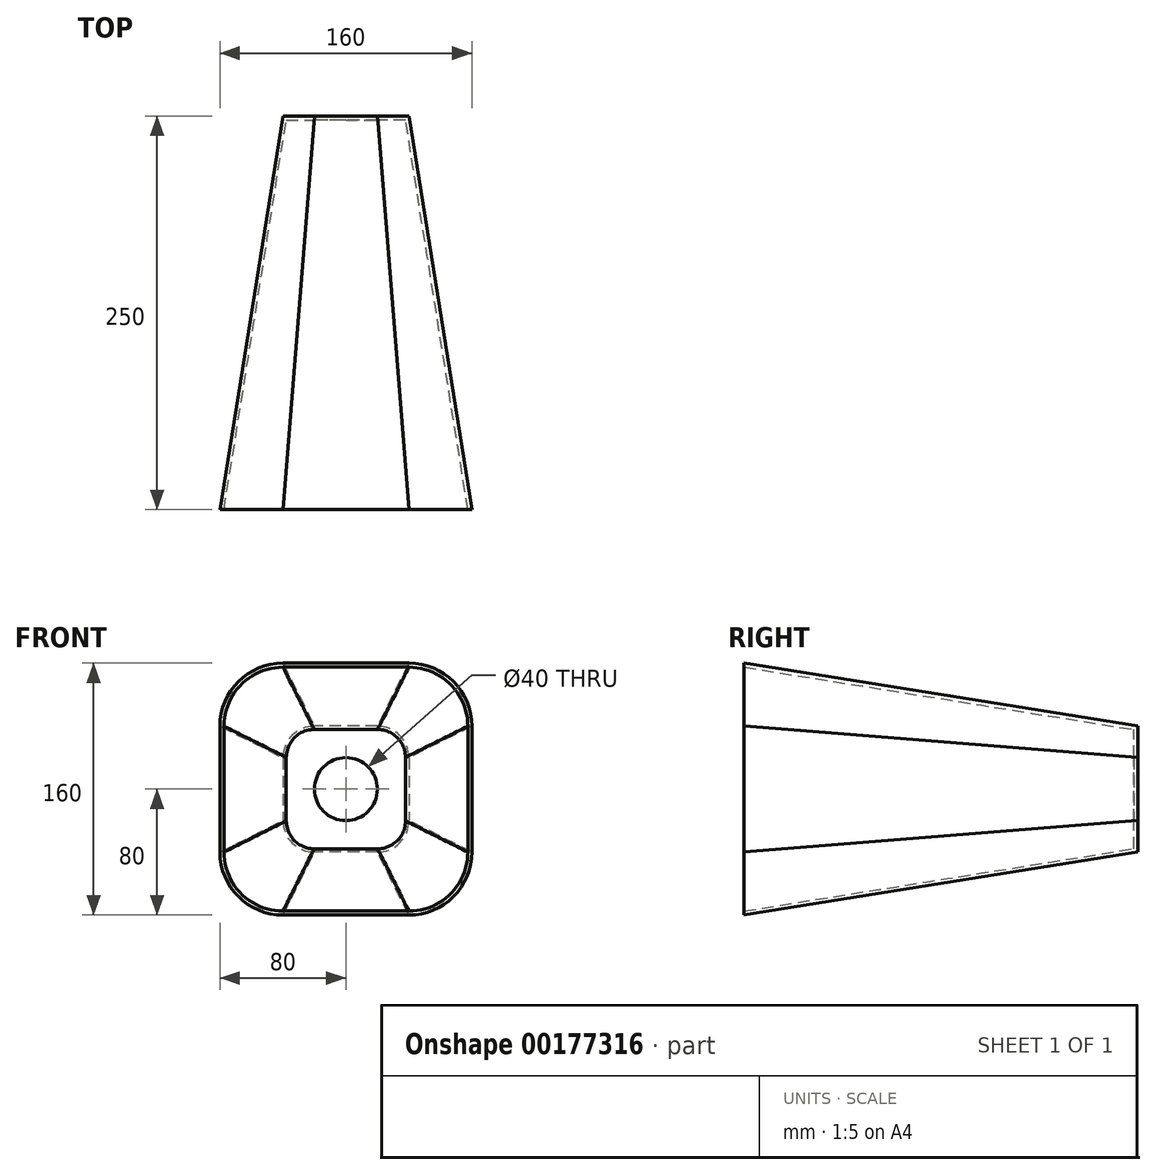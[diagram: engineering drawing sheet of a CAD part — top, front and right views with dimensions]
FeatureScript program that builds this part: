
annotation { "Feature Type Name" : "Feature", "Feature Type Description" : "" }
export const myFeature = defineFeature(function(context is Context, id is Id, definition is map)
    precondition{}
    {
        {
            var Q0;
            Q0=qCreatedBy(makeId("Front.planeOp"),FACE);
            var sketch = newSketch(context, id + "F0", { "sketchPlane" : qUnion([Q0])});
            skLineSegment(sketch, "E0.bottom", {"start": v(20, 40) * mm, "end": v(-20, 40) * mm});
            skLineSegment(sketch, "E0.top", {"start": v(20, -40) * mm, "end": v(-20, -40) * mm});
            skLineSegment(sketch, "E0.left", {"start": v(40, 20) * mm, "end": v(40, -20) * mm});
            skLineSegment(sketch, "E0.right", {"start": v(-40, 20) * mm, "end": v(-40, -20) * mm});
            skPoint(sketch, "E0.middle", {"position": v(0, 0) * mm});
            skPoint(sketch, "E1.visualSharp", {"position": v(-40, 40) * mm});
            skArc(sketch, "E1.filletArc", {"start": v(-20, 40) * mm, "mid": v(-34.14, 34.14) * mm, "end": v(-40, 20) * mm});
            skPoint(sketch, "E2.visualSharp", {"position": v(40, 40) * mm});
            skArc(sketch, "E2.filletArc", {"start": v(40, 20) * mm, "mid": v(34.14, 34.14) * mm, "end": v(20, 40) * mm});
            skPoint(sketch, "E3.visualSharp", {"position": v(40, -40) * mm});
            skArc(sketch, "E3.filletArc", {"start": v(20, -40) * mm, "mid": v(34.14, -34.14) * mm, "end": v(40, -20) * mm});
            skPoint(sketch, "E4.visualSharp", {"position": v(-40, -40) * mm});
            skArc(sketch, "E4.filletArc", {"start": v(-40, -20) * mm, "mid": v(-34.14, -34.14) * mm, "end": v(-20, -40) * mm});
            skSolve(sketch);
        }
        {
            var Q0;
            Q0=qCreatedBy(makeId("Front.planeOp"),FACE);
            cPlane(context, id + "F1", {"entities" : qUnion([Q0]), "cplaneType" : CPlaneType.OFFSET, "offset" : 250 * mm, "width" : 150 * mm, "height" : 150 * mm});
        }
        {
            var Q0;
            Q0=qCreatedBy(id+"F1.planeOp",FACE);
            var sketch = newSketch(context, id + "F2", { "sketchPlane" : qUnion([Q0])});
            skLineSegment(sketch, "E5.bottom", {"start": v(40, 80) * mm, "end": v(-40, 80) * mm});
            skLineSegment(sketch, "E5.top", {"start": v(40, -80) * mm, "end": v(-40, -80) * mm});
            skLineSegment(sketch, "E5.left", {"start": v(80, 40) * mm, "end": v(80, -40) * mm});
            skLineSegment(sketch, "E5.right", {"start": v(-80, 40) * mm, "end": v(-80, -40) * mm});
            skPoint(sketch, "E5.middle", {"position": v(0, 0) * mm});
            skPoint(sketch, "E6.visualSharp", {"position": v(80, 80) * mm});
            skArc(sketch, "E6.filletArc", {"start": v(80, 40) * mm, "mid": v(68.28, 68.28) * mm, "end": v(40, 80) * mm});
            skPoint(sketch, "E7.visualSharp", {"position": v(80, -80) * mm});
            skArc(sketch, "E7.filletArc", {"start": v(40, -80) * mm, "mid": v(68.28, -68.28) * mm, "end": v(80, -40) * mm});
            skPoint(sketch, "E8.visualSharp", {"position": v(-80, -80) * mm});
            skArc(sketch, "E8.filletArc", {"start": v(-80, -40) * mm, "mid": v(-68.28, -68.28) * mm, "end": v(-40, -80) * mm});
            skPoint(sketch, "E9.visualSharp", {"position": v(-80, 80) * mm});
            skArc(sketch, "E9.filletArc", {"start": v(-40, 80) * mm, "mid": v(-68.28, 68.28) * mm, "end": v(-80, 40) * mm});
            skSolve(sketch);
        }
        {
            var Q0;
            Q0=makeQuery(id+"F2.imprint","IMPRINT",FACE,{"disambiguationData":[TD([[makeQuery(id+"F2.imprint","IMPRINT",EDGE,{"derivedFrom":sQuery(id+"F2.wireOp",EDGE,"E5.bottom")}),1.0]])]});
            var Q1;
            Q1=makeQuery(id+"F0.imprint","IMPRINT",FACE,{"disambiguationData":[TD([[makeQuery(id+"F0.imprint","IMPRINT",EDGE,{"derivedFrom":sQuery(id+"F0.wireOp",EDGE,"E0.bottom")}),1.0]])]});
            loft(context, id + "F3", {"sheetProfilesArray" : [{ "sheetProfileEntities" : qUnion([Q0]) }, { "sheetProfileEntities" : qUnion([Q1]) }]});
        }
        {
            var Q0;
            Q0=makeQuery(id+"F3.opLoft","CAP_FACE",FACE,{"disambiguationData":[OSD([makeQuery(id+"F2.imprint","IMPRINT",FACE,{"disambiguationData":[TD([[makeQuery(id+"F2.imprint","IMPRINT",EDGE,{"derivedFrom":sQuery(id+"F2.wireOp",EDGE,"E5.bottom")}),1.0]])]})])],"isStart":true});
            shell(context, id + "F4", {"entities" : qUnion([Q0]), "thickness" : 2.5 * mm});
        }
        {
            var Q0;
            Q0=makeQuery(id+"F3.opLoft","CAP_FACE",FACE,{"disambiguationData":[OSD([makeQuery(id+"F0.imprint","IMPRINT",FACE,{"disambiguationData":[TD([[makeQuery(id+"F0.imprint","IMPRINT",EDGE,{"derivedFrom":sQuery(id+"F0.wireOp",EDGE,"E0.bottom")}),1.0]])]})])],"isStart":true});
            var sketch = newSketch(context, id + "F5", { "sketchPlane" : qUnion([Q0])});
            skCircle(sketch, "E10", {"center": v(0, 0) * mm, "radius": 20 * mm});
            skSolve(sketch);
        }
        {
            var Q0;
            Q0=makeQuery(id+"F5.imprint","IMPRINT",FACE,{"disambiguationData":[TD([[makeQuery(id+"F5.imprint","IMPRINT",EDGE,{"derivedFrom":sQuery(id+"F5.wireOp",EDGE,"E10")}),1.0]])]});
            extrude(context, id + "F6", {"entities" : qUnion([Q0]), "operationType" : NewBodyOperationType.REMOVE, "endBound" : BoundingType.UP_TO_NEXT, "oppositeDirection" : true, "depth" : 25 * mm});
        }
    });
